FCSTD DOCUMENT  (FreeCAD 1.1R20260325 (Git shallow))
Label: Tomada_Baixa_1modulo_220v_com_simbologia
License: All rights reserved
LicenseURL: http://en.wikipedia.org/wiki/All_rights_reserved
objects: Part::FeaturePython×1, Part::Feature×1, App::DocumentObjectGroup×1
note: 2 computed .brp shape members not serialized (recipe doc carries the construction recipe); baked Part::Feature solids carry a one-line shape summary decoded from their .brp

FEATURE [Part::FeaturePython] Component  label="Tomada_1modulo_110v_baixa"  # Arch/BIM 0 (typed FeaturePython)
  HorizontalArea = 0
  IfcData = attributes={"GlobalId": {"name": "GlobalId", "type": "IfcGloballyUniqueId", "is_enum": false, "enum_values": []}, "Description": {"... (+538 chars omitted),+1 more (map truncated)
  IfcType = 0
  MoveBase = false
  MoveWithHost = false
  PerimeterLength = 0
  Placement = pos=(0,0,300) rot=(0,0,1;0rad)
  PredefinedType = 0
  VerticalArea = 0
FEATURE [Part::Feature] Compound002002002004005002002003003002003005002002005002002002002002002002002002002002001  label="Simbologia_Tomada"
  Placement = pos=(702.246,2050.18,290.369) rot=(0,0,-1;1.5708rad)
  shape: bbox 86.6 x 150 x 2e-07 mm, 0 faces, 0 solids (baked)
FEATURE [App::DocumentObjectGroup] Group  label="Tomada_1modulo_baixa"
  Group = -> [Component,Compound002002002004005002002003003002003005002002005002002002002002002002002002002002001]
